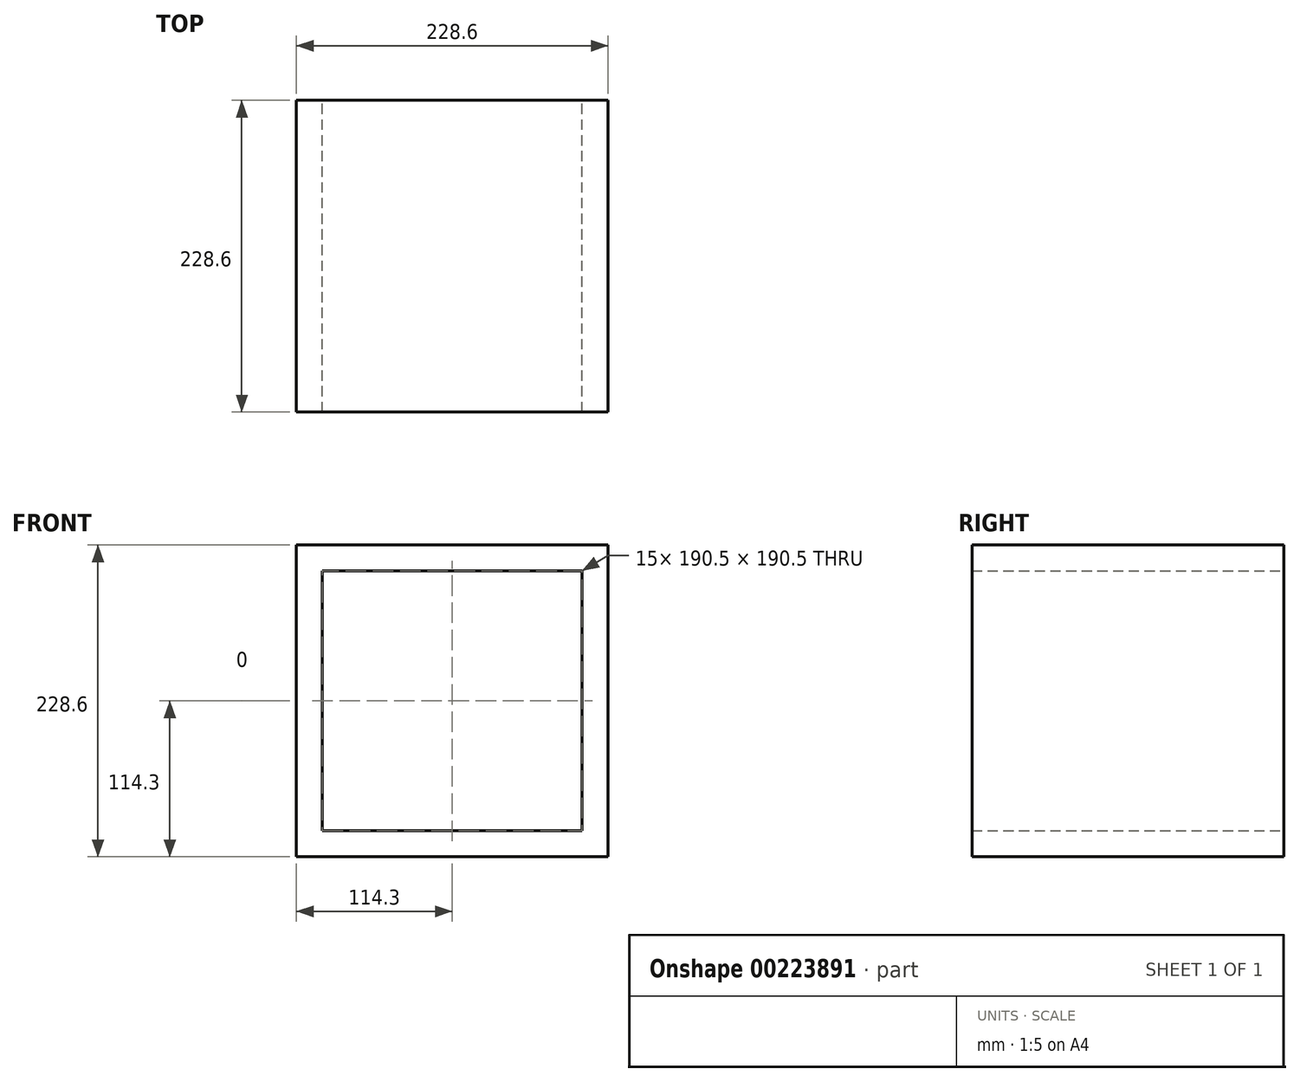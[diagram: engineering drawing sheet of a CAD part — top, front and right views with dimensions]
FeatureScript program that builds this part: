
annotation { "Feature Type Name" : "Feature", "Feature Type Description" : "" }
export const myFeature = defineFeature(function(context is Context, id is Id, definition is map)
    precondition{}
    {
        {
            var Q0;
            Q0=qCreatedBy(makeId("Front.planeOp"),FACE);
            var sketch = newSketch(context, id + "F0", { "sketchPlane" : qUnion([Q0])});
            skLineSegment(sketch, "E0.bottom", {"start": v(95.25, -95.25) * mm, "end": v(-95.25, -95.25) * mm});
            skLineSegment(sketch, "E0.top", {"start": v(95.25, 95.25) * mm, "end": v(-95.25, 95.25) * mm});
            skLineSegment(sketch, "E0.left", {"start": v(95.25, -95.25) * mm, "end": v(95.25, 95.25) * mm});
            skLineSegment(sketch, "E0.right", {"start": v(-95.25, -95.25) * mm, "end": v(-95.25, 95.25) * mm});
            skPoint(sketch, "E0.middle", {"position": v(0, 0) * mm});
            skLineSegment(sketch, "E1.bottom", {"start": v(114.3, -114.3) * mm, "end": v(-114.3, -114.3) * mm});
            skLineSegment(sketch, "E1.top", {"start": v(114.3, 114.3) * mm, "end": v(-114.3, 114.3) * mm});
            skLineSegment(sketch, "E1.left", {"start": v(114.3, -114.3) * mm, "end": v(114.3, 114.3) * mm});
            skLineSegment(sketch, "E1.right", {"start": v(-114.3, -114.3) * mm, "end": v(-114.3, 114.3) * mm});
            skSolve(sketch);
        }
        {
            var Q0;
            Q0 = qSketchRegion(id + "F0", true);
            extrude(context, id + "F1", {"entities" : qUnion([Q0]), "depth" : 228.6 * mm});
        }
    });
